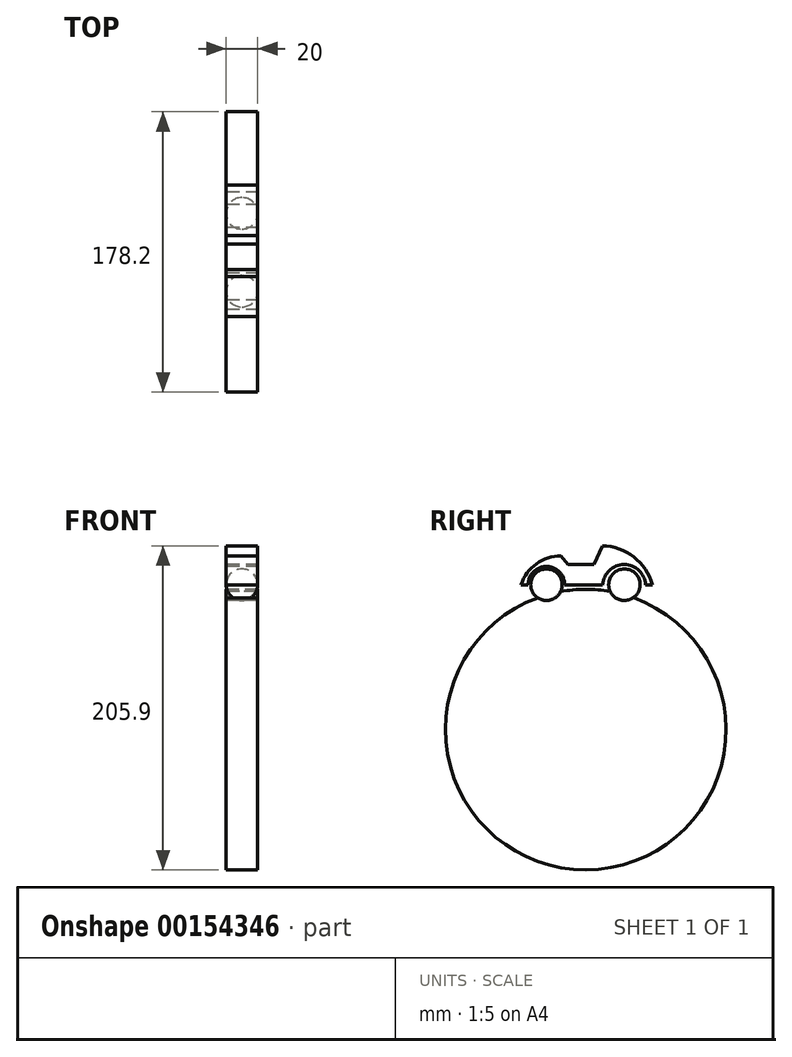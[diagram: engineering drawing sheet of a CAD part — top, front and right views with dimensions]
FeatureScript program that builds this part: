
annotation { "Feature Type Name" : "Feature", "Feature Type Description" : "" }
export const myFeature = defineFeature(function(context is Context, id is Id, definition is map)
    precondition{}
    {
        {
            var Q0;
            Q0=qCreatedBy(makeId("Right.planeOp"),FACE);
            var sketch = newSketch(context, id + "F0", { "sketchPlane" : qUnion([Q0])});
            skCircle(sketch, "E0", {"center": v(-38.78, 0) * mm, "radius": 10 * mm});
            skArc(sketch, "E1", {"start": v(-27.44, -2.39) * mm, "mid": v(-37.6, 11.55) * mm, "end": v(-50.41, 0) * mm});
            skCircle(sketch, "E2", {"center": v(10.74, 0) * mm, "radius": 10 * mm});
            skLineSegment(sketch, "E3", {"start": v(-27.44, -2.39) * mm, "end": v(-2.98, -2.39) * mm});
            skArc(sketch, "E4", {"start": v(24.16, 0) * mm, "mid": v(9.36, 12.78) * mm, "end": v(-2.98, -2.39) * mm});
            skArc(sketch, "E5", {"start": v(-29.53, 18.2) * mm, "mid": v(-45.17, 13.23) * mm, "end": v(-54.89, 0) * mm});
            skLineSegment(sketch, "E6", {"start": v(-29.53, 18.2) * mm, "end": v(-25.06, 12.83) * mm});
            skLineSegment(sketch, "E7", {"start": v(-25.06, 12.83) * mm, "end": v(-8.65, 12.83) * mm});
            skLineSegment(sketch, "E8", {"start": v(-8.65, 12.83) * mm, "end": v(-3.28, 24.76) * mm});
            skArc(sketch, "E9", {"start": v(28.64, 0) * mm, "mid": v(16.68, 17.55) * mm, "end": v(-3.28, 24.76) * mm});
            skLineSegment(sketch, "E10", {"start": v(24.16, 0) * mm, "end": v(28.64, 0) * mm});
            skLineSegment(sketch, "E11", {"start": v(-54.89, 0) * mm, "end": v(-50.41, 0) * mm});
            skLineSegment(sketch, "E12", {"start": v(-38.78, 0) * mm, "end": v(10.74, 0) * mm});
            skLineSegment(sketch, "E13", {"start": v(10.74, 0) * mm, "end": v(20.74, 0) * mm});
            skLineSegment(sketch, "E14", {"start": v(-38.78, 0) * mm, "end": v(-48.78, 0) * mm});
            skArc(sketch, "E15", {"start": v(11.1, -6.5) * mm, "mid": v(-13.92, -2.94) * mm, "end": v(-38.94, -6.55) * mm});
            skCircle(sketch, "E16", {"center": v(-13.81, -92.04) * mm, "radius": 89.1 * mm});
            skSolve(sketch);
        }
        {
            var Q0;
            {var subQ0=sQuery(id+"F0.wireOp",EDGE,"E14");Q0=makeQuery(id+"F0.imprint","IMPRINT",FACE,{"disambiguationData":[TD([[makeQuery(id+"F0.imprint","IMPRINT",EDGE,{"derivedFrom":subQ0}),-1.0]])]});}
            var Q1;
            {var subQ0=sQuery(id+"F0.wireOp",EDGE,"E13");Q1=makeQuery(id+"F0.imprint","IMPRINT",FACE,{"disambiguationData":[TD([[makeQuery(id+"F0.imprint","IMPRINT",EDGE,{"derivedFrom":subQ0}),1.0]])]});}
            var Q2;
            Q2=sQuery(id+"F0.wireOp",EDGE,"E12");
            revolve(context, id + "F1", {"entities" : qUnion([Q0, Q1]), "axis" : qUnion([Q2]), "revolveType" : RevolveType.FULL});
        }
        {
            var Q0;
            Q0=makeQuery(id+"F0.imprint","IMPRINT",FACE,{"disambiguationData":[TD([[makeQuery(id+"F0.imprint","IMPRINT",EDGE,{"derivedFrom":sQuery(id+"F0.wireOp",EDGE,"E5")}),1.0]])]});
            extrude(context, id + "F2", {"entities" : qUnion([Q0]), "depth" : 10 * mm, "hasSecondDirection" : true, "secondDirectionOppositeDirection" : true, "secondDirectionDepth" : 10 * mm});
        }
        {
            var Q0;
            {var subQ0=sQuery(id+"F0.wireOp",EDGE,"E16");var subQ1=sQuery(id+"F0.wireOp",EDGE,"E0");var subQ2=makeQuery(id+"F0.imprint","INTERSECT",VERTEX,{"disambiguationData":[OD(0.0)],"derivedFrom":[subQ1,subQ0]});Q0=makeQuery(id+"F0.imprint","IMPRINT",FACE,{"disambiguationData":[TD([[makeQuery(id+"F0.imprint","IMPRINT",EDGE,{"disambiguationData":[TD([[subQ2,-1.0]])],"derivedFrom":subQ1}),-1.0]])]});}
            var Q1;
            {var subQ0=sQuery(id+"F0.wireOp",EDGE,"E16");var subQ4=makeQuery(id+"F0.imprint","IMPRINT",VERTEX,{"disambiguationData":[OD(1.0)],"derivedFrom":subQ0});Q1=makeQuery(id+"F0.imprint","IMPRINT",FACE,{"disambiguationData":[TD([[makeQuery(id+"F0.imprint","IMPRINT",EDGE,{"disambiguationData":[TD([[subQ4,1.0]])],"derivedFrom":subQ0}),1.0]])]});}
            var Q2;
            {var subQ0=sQuery(id+"F0.wireOp",EDGE,"E16");var subQ4=makeQuery(id+"F0.imprint","IMPRINT",VERTEX,{"disambiguationData":[OD(0.0)],"derivedFrom":subQ0});Q2=makeQuery(id+"F0.imprint","IMPRINT",FACE,{"disambiguationData":[TD([[makeQuery(id+"F0.imprint","IMPRINT",EDGE,{"disambiguationData":[TD([[subQ4,1.0]])],"derivedFrom":subQ0}),1.0]])]});}
            extrude(context, id + "F3", {"entities" : qUnion([Q0, Q1, Q2]), "depth" : 10 * mm, "hasSecondDirection" : true, "secondDirectionOppositeDirection" : true, "secondDirectionDepth" : 10 * mm});
        }
    });
